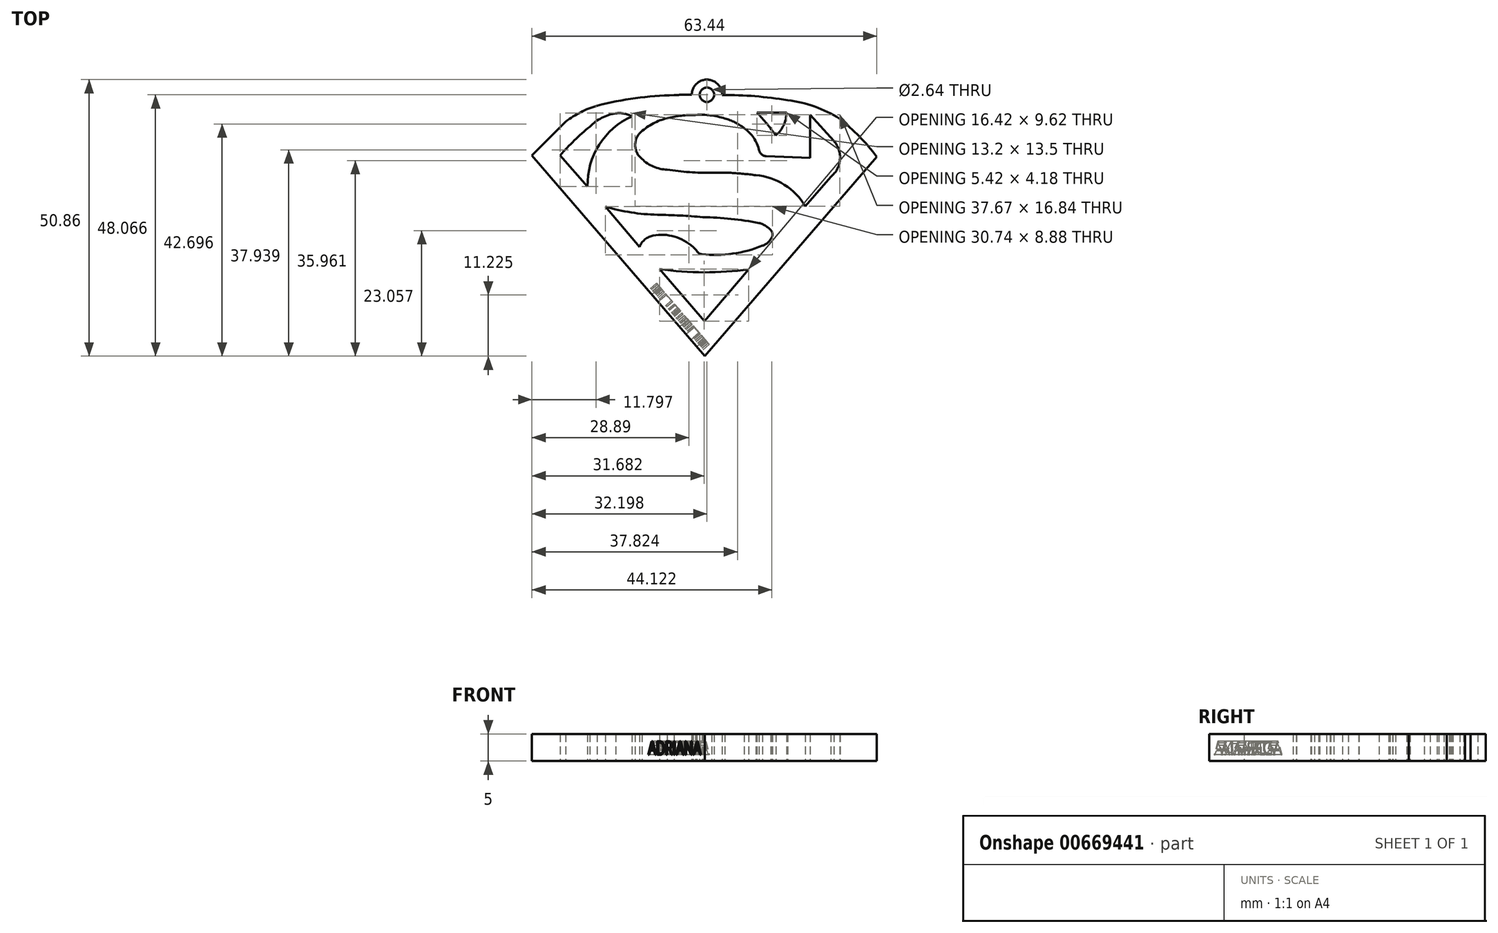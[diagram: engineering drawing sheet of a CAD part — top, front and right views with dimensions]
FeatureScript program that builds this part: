
annotation { "Feature Type Name" : "Feature", "Feature Type Description" : "" }
export const myFeature = defineFeature(function(context is Context, id is Id, definition is map)
    precondition{}
    {
        {
            var Q0;
            Q0=qCreatedBy(makeId("Top.planeOp"),FACE);
            var sketch = newSketch(context, id + "F0", { "sketchPlane" : qUnion([Q0])});
            skLineSegment(sketch, "E0", {"start": v(100, 0) * mm, "end": v(-100, 0) * mm, "construction": true});
            skLineSegment(sketch, "E1", {"start": v(0, 100) * mm, "end": v(0, -100) * mm, "construction": true});
            skLineSegment(sketch, "E2", {"start": v(24.68, 16.9) * mm, "end": v(32.93, 7.28) * mm});
            skLineSegment(sketch, "E3", {"start": v(32.93, 7.28) * mm, "end": v(41.1, 16.84) * mm});
            skArc(sketch, "E4", {"start": v(24.68, 16.9) * mm, "mid": v(32.89, 16.28) * mm, "end": v(41.1, 16.84) * mm});
            skArc(sketch, "E5", {"start": v(14.73, 28.37) * mm, "mid": v(19.46, 27.3) * mm, "end": v(24.28, 26.87) * mm});
            skArc(sketch, "E6", {"start": v(32.65, 26.43) * mm, "mid": v(28.47, 26.73) * mm, "end": v(24.28, 26.87) * mm});
            skArc(sketch, "E7", {"start": v(42.97, 25.36) * mm, "mid": v(37.83, 26.1) * mm, "end": v(32.65, 26.43) * mm});
            skArc(sketch, "E8", {"start": v(45.37, 23.74) * mm, "mid": v(44.3, 24.75) * mm, "end": v(42.97, 25.36) * mm});
            skArc(sketch, "E9", {"start": v(45.15, 22.43) * mm, "mid": v(45.45, 23.05) * mm, "end": v(45.37, 23.74) * mm});
            skArc(sketch, "E10", {"start": v(43.62, 21.17) * mm, "mid": v(44.51, 21.65) * mm, "end": v(45.15, 22.43) * mm});
            skLineSegment(sketch, "E11", {"start": v(14.73, 28.37) * mm, "end": v(21, 20.95) * mm});
            skArc(sketch, "E12", {"start": v(23.51, 23.05) * mm, "mid": v(22, 22.32) * mm, "end": v(21, 20.95) * mm});
            skArc(sketch, "E13", {"start": v(30.83, 20.95) * mm, "mid": v(27.41, 22.85) * mm, "end": v(23.51, 23.05) * mm});
            skArc(sketch, "E14", {"start": v(31.56, 20.18) * mm, "mid": v(31.21, 20.59) * mm, "end": v(30.83, 20.95) * mm});
            skArc(sketch, "E15", {"start": v(31.56, 20.18) * mm, "mid": v(31.95, 19.79) * mm, "end": v(32.47, 19.62) * mm});
            skArc(sketch, "E16", {"start": v(32.47, 19.62) * mm, "mid": v(38.14, 19.7) * mm, "end": v(43.62, 21.17) * mm});
            skArc(sketch, "E17", {"start": v(51.5, 28.41) * mm, "mid": v(47.65, 32.4) * mm, "end": v(42.4, 34.14) * mm});
            skArc(sketch, "E18", {"start": v(42.4, 34.14) * mm, "mid": v(40.11, 34.4) * mm, "end": v(37.82, 34.58) * mm});
            skArc(sketch, "E19", {"start": v(37.82, 34.58) * mm, "mid": v(36.06, 34.63) * mm, "end": v(34.3, 34.58) * mm});
            skLineSegment(sketch, "E20", {"start": v(51.5, 28.41) * mm, "end": v(56.2, 33.85) * mm});
            skArc(sketch, "E21", {"start": v(56.2, 33.85) * mm, "mid": v(57.87, 37.01) * mm, "end": v(56.77, 40.42) * mm});
            skLineSegment(sketch, "E22", {"start": v(56.77, 40.42) * mm, "end": v(52.36, 45.24) * mm});
            skLineSegment(sketch, "E23", {"start": v(52.36, 45.24) * mm, "end": v(52.36, 37.3) * mm});
            skLineSegment(sketch, "E24", {"start": v(52.36, 37.3) * mm, "end": v(44.33, 37.62) * mm});
            skArc(sketch, "E25", {"start": v(43, 38.7) * mm, "mid": v(43.49, 37.94) * mm, "end": v(44.33, 37.62) * mm});
            skArc(sketch, "E26", {"start": v(43, 38.7) * mm, "mid": v(42, 41) * mm, "end": v(40.24, 42.8) * mm});
            skArc(sketch, "E27", {"start": v(40.24, 42.8) * mm, "mid": v(38.57, 43.87) * mm, "end": v(36.7, 44.56) * mm});
            skArc(sketch, "E28", {"start": v(36.7, 44.56) * mm, "mid": v(34.05, 45.15) * mm, "end": v(31.33, 45.22) * mm});
            skArc(sketch, "E29", {"start": v(31.33, 45.22) * mm, "mid": v(28.69, 45.1) * mm, "end": v(26.1, 44.62) * mm});
            skArc(sketch, "E30", {"start": v(26.1, 44.62) * mm, "mid": v(23.53, 43.66) * mm, "end": v(21.28, 42.1) * mm});
            skArc(sketch, "E31", {"start": v(21.28, 42.1) * mm, "mid": v(20.2, 39.58) * mm, "end": v(21.44, 37.15) * mm});
            skArc(sketch, "E32", {"start": v(21.44, 37.15) * mm, "mid": v(23.58, 35.7) * mm, "end": v(26.1, 35.16) * mm});
            skArc(sketch, "E33", {"start": v(26.1, 35.16) * mm, "mid": v(30.19, 34.71) * mm, "end": v(34.3, 34.58) * mm});
            skLineSegment(sketch, "E34", {"start": v(42.62, 45.65) * mm, "end": v(48.04, 45.65) * mm});
            skArc(sketch, "E35", {"start": v(46.08, 41.48) * mm, "mid": v(47.53, 43.35) * mm, "end": v(48.04, 45.65) * mm});
            skArc(sketch, "E36", {"start": v(46.08, 41.48) * mm, "mid": v(44.42, 43.62) * mm, "end": v(42.62, 45.65) * mm});
            skArc(sketch, "E37", {"start": v(19.6, 44.98) * mm, "mid": v(13.58, 39.75) * mm, "end": v(11.45, 32.06) * mm});
            skArc(sketch, "E38", {"start": v(19.6, 44.98) * mm, "mid": v(18.17, 45.48) * mm, "end": v(16.64, 45.52) * mm});
            skArc(sketch, "E39", {"start": v(16.64, 45.52) * mm, "mid": v(14.05, 44.68) * mm, "end": v(11.85, 43.07) * mm});
            skArc(sketch, "E40", {"start": v(11.85, 43.07) * mm, "mid": v(9.02, 40.54) * mm, "end": v(6.4, 37.8) * mm});
            skLineSegment(sketch, "E41", {"start": v(6.4, 37.8) * mm, "end": v(11.45, 32.06) * mm});
            skLineSegment(sketch, "E42", {"start": v(1.2, 37.8) * mm, "end": v(33.04, 0.87) * mm});
            skLineSegment(sketch, "E43", {"start": v(33.04, 0.87) * mm, "end": v(64.65, 37.54) * mm});
            skArc(sketch, "E44", {"start": v(64.65, 37.54) * mm, "mid": v(61.45, 41.24) * mm, "end": v(57.82, 44.52) * mm});
            skArc(sketch, "E45", {"start": v(57.82, 44.52) * mm, "mid": v(53.23, 46.77) * mm, "end": v(48.25, 47.93) * mm});
            skArc(sketch, "E46", {"start": v(48.25, 47.93) * mm, "mid": v(42.25, 48.67) * mm, "end": v(36.2, 48.9) * mm});
            skLineSegment(sketch, "E47", {"start": v(1.2, 37.8) * mm, "end": v(7.44, 44) * mm});
            skArc(sketch, "E48", {"start": v(13.2, 46.94) * mm, "mid": v(10.19, 45.73) * mm, "end": v(7.44, 44) * mm});
            skArc(sketch, "E49", {"start": v(27.37, 48.88) * mm, "mid": v(20.24, 48.31) * mm, "end": v(13.2, 46.94) * mm});
            skArc(sketch, "E50", {"start": v(34.79, 48.88) * mm, "mid": v(34.76, 48.88) * mm, "end": v(34.73, 48.88) * mm});
            skArc(sketch, "E51", {"start": v(36.2, 48.9) * mm, "mid": v(33.44, 51.73) * mm, "end": v(30.61, 48.97) * mm});
            skCircle(sketch, "E52", {"center": v(33.4, 48.94) * mm, "radius": 1.32 * mm});
            skArc(sketch, "E53.trimOffspring", {"start": v(30.61, 48.97) * mm, "mid": v(29, 48.94) * mm, "end": v(27.37, 48.88) * mm});
            skSolve(sketch);
        }
        {
            var Q0;
            Q0 = qSketchRegion(id + "F0", true);
            extrude(context, id + "F1", {"entities" : qUnion([Q0]), "depth" : 5 * mm, "offsetDistance" : 25 * mm});
        }
        {
            var Q0;
            Q0=makeQuery(id+"F1.opExtrude","SWEPT_FACE",FACE,{"disambiguationData":[OSD([sQuery(id+"F0.wireOp",EDGE,"E42")])]});
            var sketch = newSketch(context, id + "F2", { "sketchPlane" : qUnion([Q0])});
            skText(sketch, "E54", { "text": "ADRIANA", "fontName": "OpenSans-Regular.ttf"});
            const initialGuessF2  = {"E54": [0.00495, 0.00115, 1, 0, 0.0025]};
            skSetInitialGuess(sketch, initialGuessF2);
            skSolve(sketch);
        }
        {
            var Q0;
            Q0 = qSketchRegion(id + "F2", true);
            extrude(context, id + "F3", {"entities" : qUnion([Q0]), "operationType" : NewBodyOperationType.REMOVE, "oppositeDirection" : true, "depth" : 2 * mm, "offsetDistance" : 25 * mm});
        }
    });
